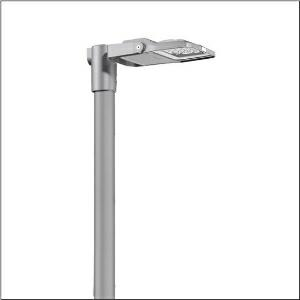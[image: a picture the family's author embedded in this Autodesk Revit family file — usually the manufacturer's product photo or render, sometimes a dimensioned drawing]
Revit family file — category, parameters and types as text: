
# Revit family: floodlight_fl_21_iq_micro___pl43_5xa7762a2a3a_62d6
name_source: partatom
category: Lighting Fixtures
units: mm (PartAtom-declared; Revit-internal decimal feet)

## family parameters
Cut with Voids When Loaded = No
Host = Face
Light Source = No
Part Type = Normal
Room Calculation Point = No
Round Connector Dimension = Use Diameter
Shared = No

## types (1)
- --- (1 x LED, 3040 lm, 23.1 W, 3000K)
    Apparent Load = 23 VA
    CIE Flux Codes = 29 80 99 100 100
    Color Rendering = 70
    Color Temperature = 3000K
    Default Elevation = 1800 mm
    Description = Floodlight FL 21 iQ micro, floodlight, primary light control with lens, of PMMA, primary optical cover: protective disc, of toughened safety glass, transparent, light distribution: PL43, light emission: direct distribution, installation type: surface-mounted, lamps: LED, High Power LED, rated values: 3.040lm | 23,1W | 131,6lm/W (begin service life); end service life: 3.040lm | 23,8W; at 50% lumin. flux: 1.520lm | 11W | 138,2lm/W, colour temperature: 3000K, colour rendering: CRI > 70, light colour: 730, light setting 1 begin service life: 100% | 3.040lm | 23,1W | 131,6lm/W | 3.000K, light setting 1 end service life: 23,8W, further light settings possible, control: Auto-Match, Temp-Guard, Night-Set, Smart-Wire, Desk-Remote (wireless, voltage-free reading and setting of iQ features in the workshop via application-optimized NFC function/RFID function), optimised constant luminous flux control (CLO 2.0), Street-Remote, pre-setting: linear dimming characteristic, with terminal, 6-pole, mains connection: 220..240V, AC, 50/60Hz, luminaire housing, of diecast aluminium, powder-coated, SITECO metallic grey (DB 702S), corrosivity category C5 mid according to DIN EN ISO 12944suitable for swimming poolschlorine-resistant, sealing non-destructively replaceable, please order mast flange separately, mast bracket, of steel, galvanised, powder-coated, SITECO metallic grey (DB 702S), protection rating (complete): IP66, insulation class (complete): insulation class II (safety insulation), certification: CE, ENEC, VDE, protection symbol: D, impact resistance: IK07, permissible operating ambient temperature: -40..+40°C, permissible operating ambient temperature for outdoor applications: -40..+50°C, standard: DIN EN 12944, LABS conformity tested according to VDMA 24364:2018-05, packaging unit: 1 piece

Light Distribution: PL43
    Height = 65 mm
    Lamp = 1 x LED
    Lamp Light Flux = 3040 lm
    Lamp Power = 23.1 W
    Lamp count = 1
    Length = 312 mm
    Luminous efficacy = 132 lm/W
    Manufacturer = Siteco
    ModVariant = No
    Model = 5XA7762A2A3A
    Number of Poles = 1
    OnlyDefault = Yes
    Power Factor = 1
    Product Name = Floodlight FL 21 iQ micro | PL43
    Product group = floodlight | pylon annexe
    ProductGroupID = 6201
    Protection Class = Protection class II
    Protection Degree = IP 66
    RLX_Detail_Level = 1
    RLX_Emergency_Light_Flux = 0 lm
    RLX_Emergency_Type = 0
    RLX_Emergency_Type_DB = No
    RlxData = <blob elided: 102005 chars, md5=7baf3270>
    Socket = socket
    Standby Power = 0 W
    System Light Flux = 3040 lm
    System Power = 23 W
    Type Comments = factory setting: luminous flux: 100 % | dim-lin: 254 | 455 mA
    Type Image = l_1007121.jpg
    URL = http://relux.com
    VarID = @adj_176061
    Voltage = 0 V
    Weight = 0.00 kg
    Width = 230 mm

## geometry (parser evidence)
native form markers: Blend x4, Sweep x13
no freeform markers — native parametric forms only
